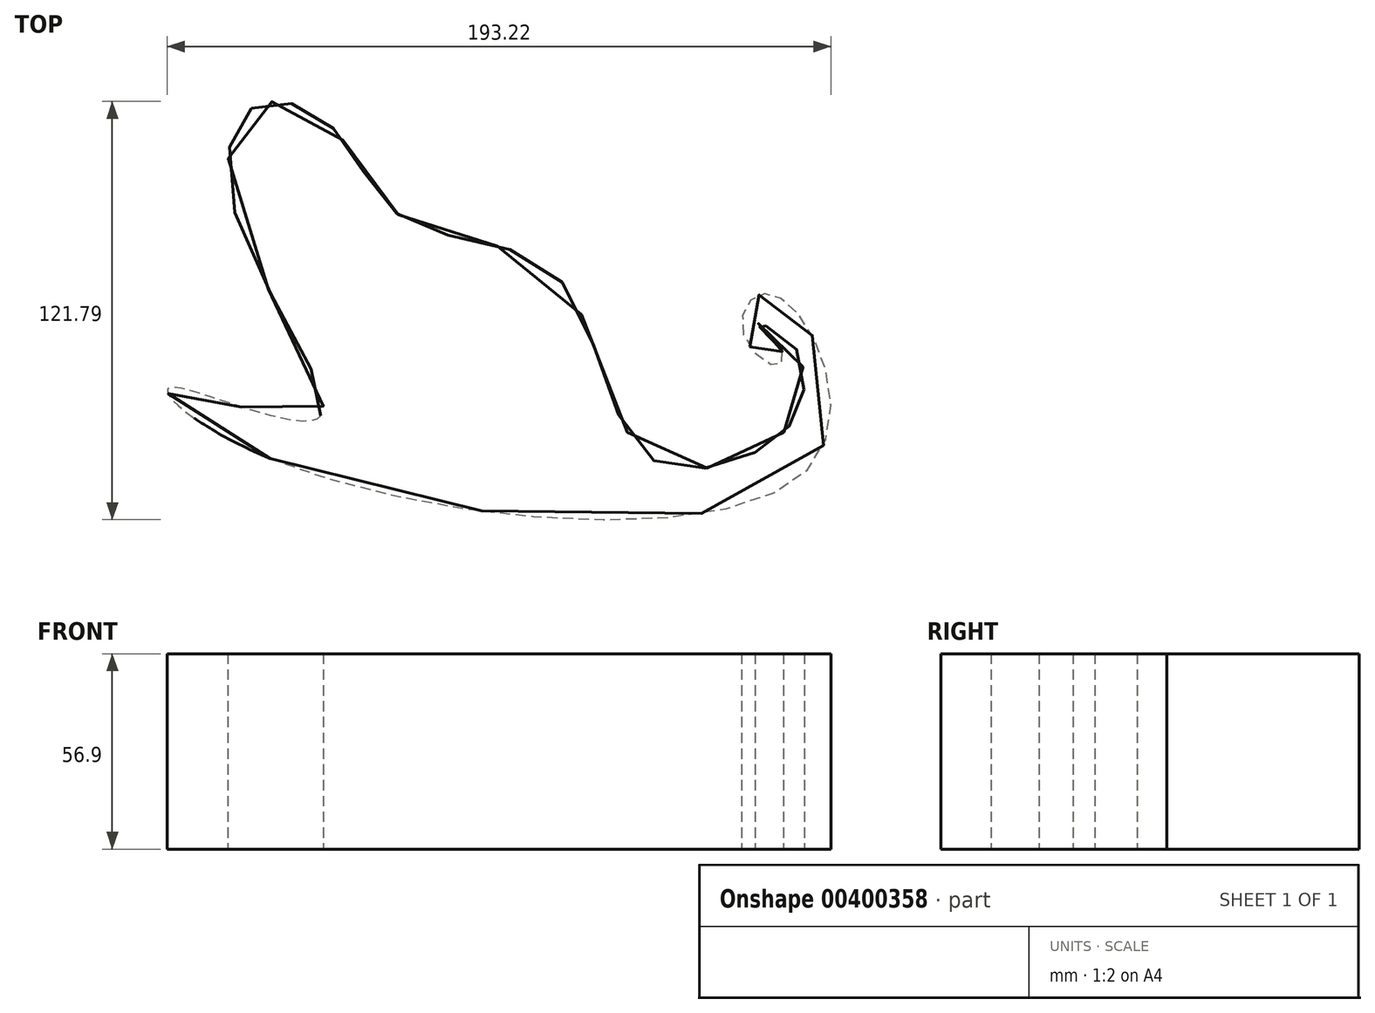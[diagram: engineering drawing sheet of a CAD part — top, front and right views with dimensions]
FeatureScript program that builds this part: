
annotation { "Feature Type Name" : "Feature", "Feature Type Description" : "" }
export const myFeature = defineFeature(function(context is Context, id is Id, definition is map)
    precondition{}
    {
        {
            var Q0;
            Q0=qCreatedBy(makeId("Top.planeOp"),FACE);
            var sketch = newSketch(context, id + "F0", { "sketchPlane" : qUnion([Q0])});
            skFitSpline(sketch, "E0", {"points": [v(-98.05, -20.66) * mm, v(58.34, -24.12) * mm, v(56.78, 20.1) * mm, v(43.8, 26.7) * mm, v(39.84, 15.25) * mm, v(50.22, 6.43) * mm, v(49.8, 13.25) * mm, v(43.2, 18.6) * mm, v(52.76, 14.24) * mm, v(56.63, -4.67) * mm, v(41.93, -19.5) * mm, v(10.73, -19.19) * mm, v(-15.1, 32.87) * mm, v(-58.45, 48.74) * mm, v(-80.04, 75.75) * mm, v(-102.3, 81.94) * mm, v(-107.37, 47.99) * mm, v(-84.24, -9.16) * mm, v(-126.51, 0) * mm, v(-98.05, -20.66) * mm]});
            skSolve(sketch);
        }
        {
            var Q0;
            Q0 = qSketchRegion(id + "F0", true);
            extrude(context, id + "F1", {"entities" : qUnion([Q0]), "depth" : 56.9 * mm});
        }
    });
